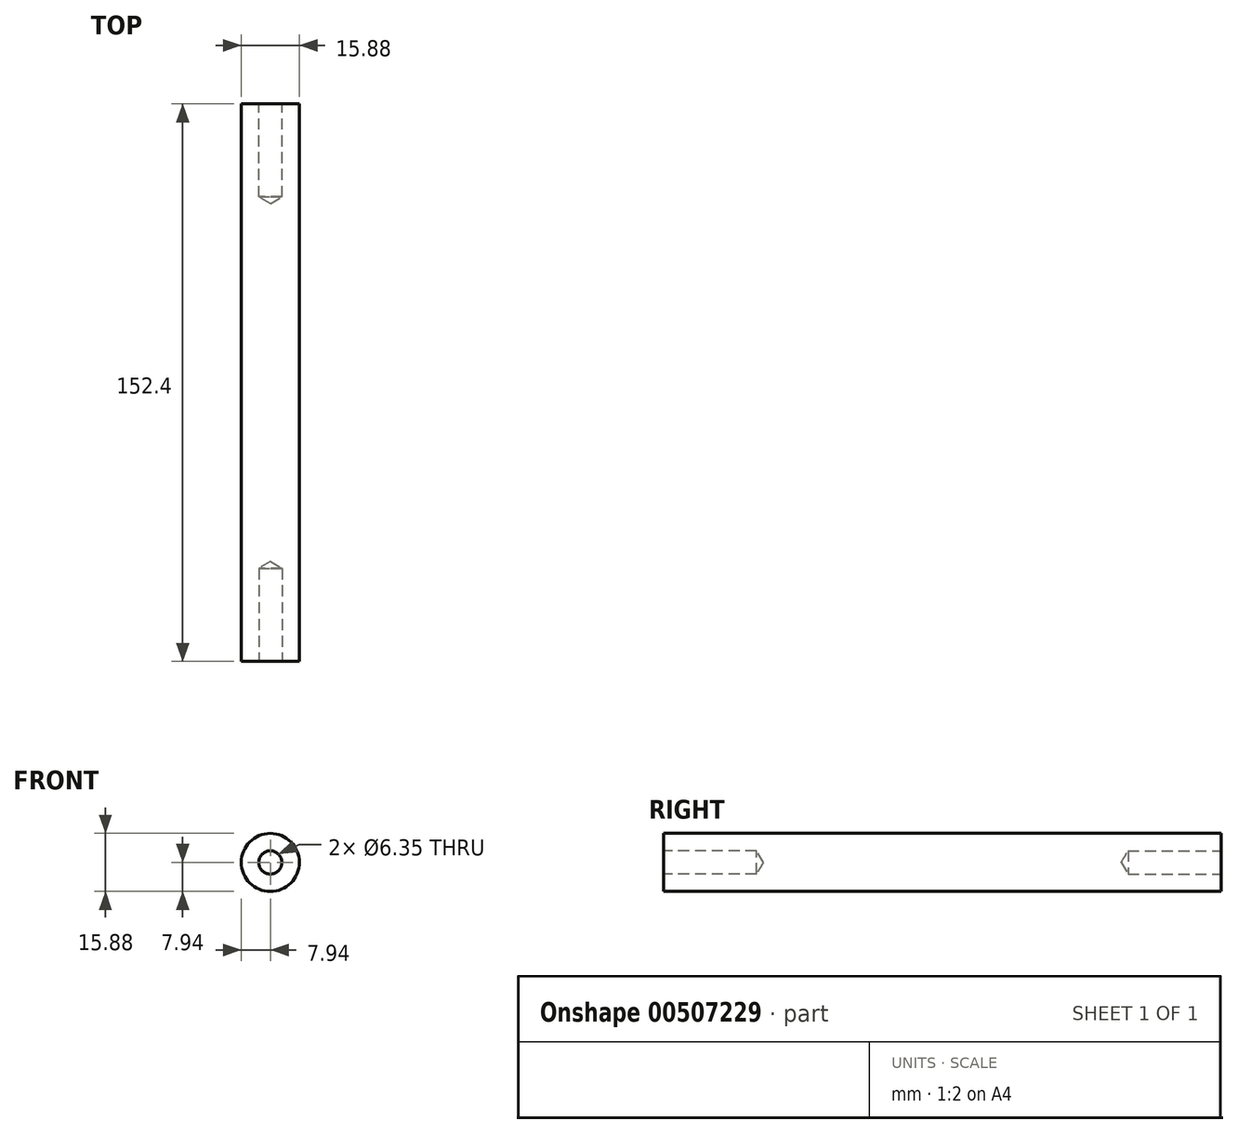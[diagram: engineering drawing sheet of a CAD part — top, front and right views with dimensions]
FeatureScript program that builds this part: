
annotation { "Feature Type Name" : "Feature", "Feature Type Description" : "" }
export const myFeature = defineFeature(function(context is Context, id is Id, definition is map)
    precondition{}
    {
        {
            var Q0;
            Q0=qCreatedBy(makeId("Front.planeOp"),FACE);
            var sketch = newSketch(context, id + "F0", { "sketchPlane" : qUnion([Q0])});
            skCircle(sketch, "E0", {"center": v(0, 0) * mm, "radius": 7.94 * mm});
            skSolve(sketch);
        }
        {
            var Q0;
            Q0=makeQuery(id+"F0.imprint","IMPRINT",FACE,{"disambiguationData":[TD([[makeQuery(id+"F0.imprint","IMPRINT",EDGE,{"derivedFrom":sQuery(id+"F0.wireOp",EDGE,"E0")}),1.0]])]});
            extrude(context, id + "F1", {"entities" : qUnion([Q0]), "depth" : 152.4 * mm});
        }
        {
            var Q0;
            Q0=makeQuery(id+"F1.opExtrude","CAP_FACE",FACE,{"disambiguationData":[OSD([sQuery(id+"F0.wireOp",EDGE,"E0")])],"isStart":false});
            var sketch = newSketch(context, id + "F2", { "sketchPlane" : qUnion([Q0])});
            skPoint(sketch, "E1", {"position": v(0, 0) * mm});
            skSolve(sketch);
        }
        {
            var Q0;
            Q0=sQuery(id+"F2.wireOp",VERTEX,"E1");
            var Q1;
            Q1=makeQuery(id+"F1.opExtrude","SWEPT_BODY",BODY,{"disambiguationData":[OSD([sQuery(id+"F0.wireOp",EDGE,"E0")])]});
            hole(context, id + "F3", {"style" : HoleStyle.SIMPLE, "endStyle" : HoleEndStyle.BLIND, "holeDiameter" : 6.35 * mm, "holeDepth" : 25.4 * mm, "isTappedThrough" : true, "tappedDepth" : 12.7 * mm, "tapClearance" : 3, "startFromSketch" : true, "locations" : qUnion([Q0]), "scope" : qUnion([Q1])});
        }
        {
            var Q0;
            Q0=makeQuery(id+"F1.opExtrude","CAP_FACE",FACE,{"disambiguationData":[OSD([sQuery(id+"F0.wireOp",EDGE,"E0")])],"isStart":true});
            var sketch = newSketch(context, id + "F4", { "sketchPlane" : qUnion([Q0])});
            skPoint(sketch, "E2", {"position": v(0, 0) * mm});
            skSolve(sketch);
        }
        {
            var Q0;
            Q0=sQuery(id+"F4.wireOp",VERTEX,"E2");
            var Q1;
            Q1=makeQuery(id+"F1.opExtrude","SWEPT_BODY",BODY,{"disambiguationData":[OSD([sQuery(id+"F0.wireOp",EDGE,"E0")])]});
            hole(context, id + "F5", {"style" : HoleStyle.SIMPLE, "endStyle" : HoleEndStyle.BLIND, "holeDiameter" : 6.35 * mm, "holeDepth" : 25.4 * mm, "isTappedThrough" : true, "tappedDepth" : 12.7 * mm, "tapClearance" : 3, "startFromSketch" : true, "locations" : qUnion([Q0]), "scope" : qUnion([Q1])});
        }
    });
